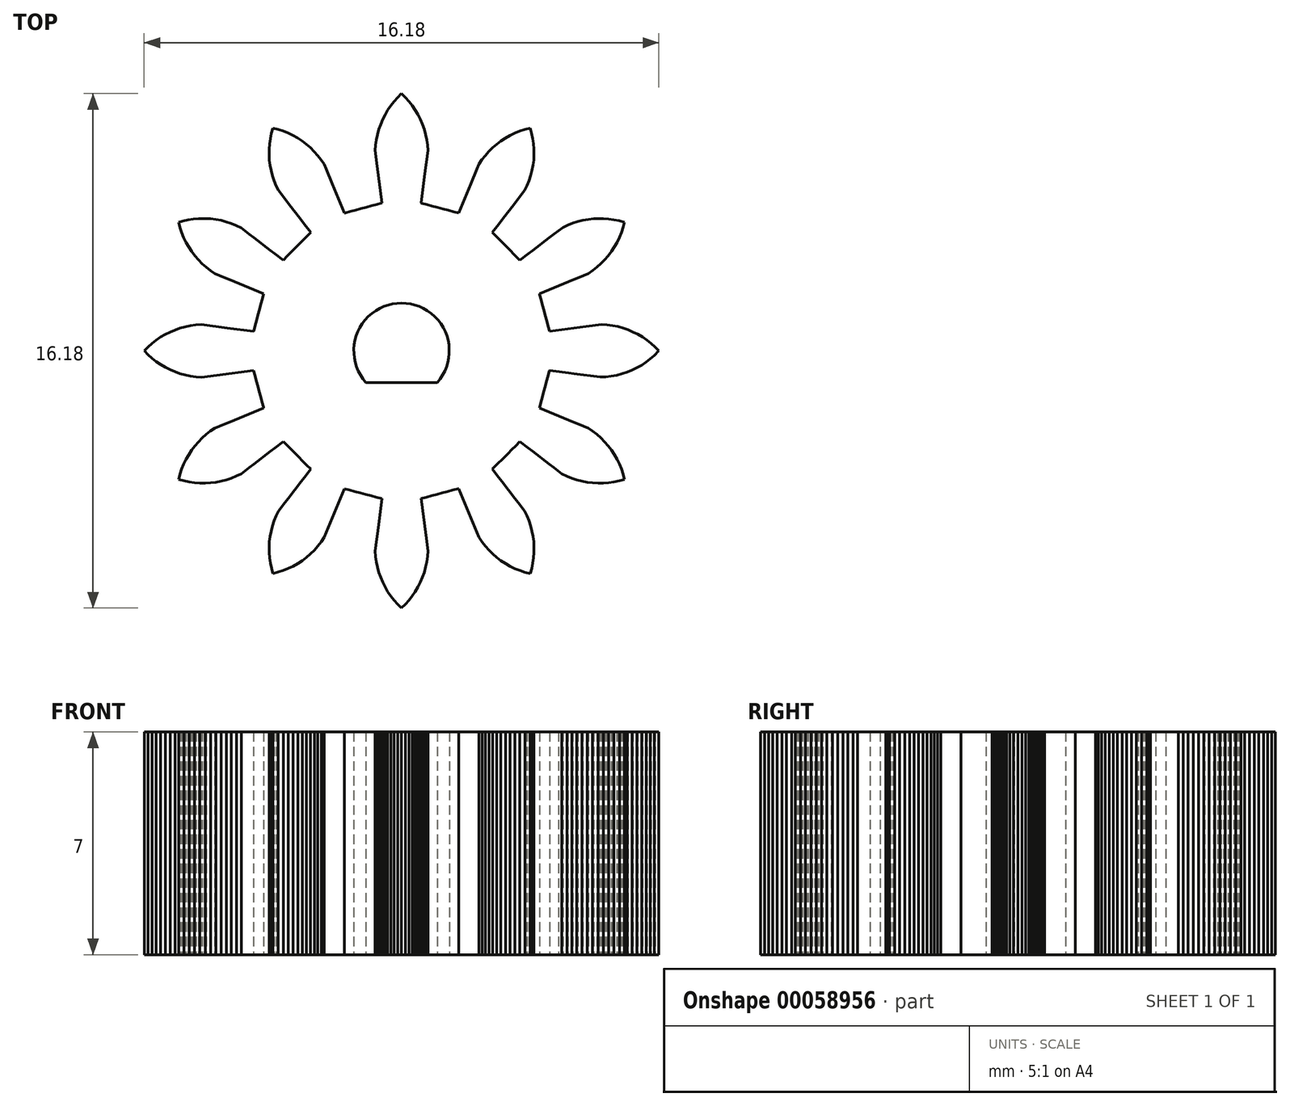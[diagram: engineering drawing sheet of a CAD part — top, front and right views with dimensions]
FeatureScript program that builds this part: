
annotation { "Feature Type Name" : "Feature", "Feature Type Description" : "" }
export const myFeature = defineFeature(function(context is Context, id is Id, definition is map)
    precondition{}
    {
        {
            var Q0;
            Q0=qCreatedBy(makeId("Top.planeOp"),FACE);
            var sketch = newSketch(context, id + "F0", { "sketchPlane" : qUnion([Q0])});
            skLineSegment(sketch, "E0", {"start": v(3.63, -0.61) * mm, "end": v(3.74, -0.63) * mm});
            skLineSegment(sketch, "E1", {"start": v(3.74, -0.63) * mm, "end": v(3.9, -0.65) * mm});
            skLineSegment(sketch, "E2", {"start": v(3.9, -0.65) * mm, "end": v(4.07, -0.67) * mm});
            skLineSegment(sketch, "E3", {"start": v(4.07, -0.67) * mm, "end": v(4.24, -0.7) * mm});
            skLineSegment(sketch, "E4", {"start": v(4.24, -0.7) * mm, "end": v(4.4, -0.71) * mm});
            skLineSegment(sketch, "E5", {"start": v(4.4, -0.71) * mm, "end": v(4.57, -0.74) * mm});
            skLineSegment(sketch, "E6", {"start": v(4.57, -0.74) * mm, "end": v(4.73, -0.76) * mm});
            skLineSegment(sketch, "E7", {"start": v(4.73, -0.76) * mm, "end": v(4.9, -0.78) * mm});
            skLineSegment(sketch, "E8", {"start": v(4.9, -0.78) * mm, "end": v(5.06, -0.8) * mm});
            skLineSegment(sketch, "E9", {"start": v(5.06, -0.8) * mm, "end": v(5.23, -0.82) * mm});
            skLineSegment(sketch, "E10", {"start": v(5.23, -0.82) * mm, "end": v(5.4, -0.82) * mm});
            skLineSegment(sketch, "E11", {"start": v(5.4, -0.82) * mm, "end": v(5.57, -0.8) * mm});
            skLineSegment(sketch, "E12", {"start": v(5.57, -0.8) * mm, "end": v(5.75, -0.77) * mm});
            skLineSegment(sketch, "E13", {"start": v(5.75, -0.77) * mm, "end": v(5.92, -0.72) * mm});
            skLineSegment(sketch, "E14", {"start": v(5.92, -0.72) * mm, "end": v(6.07, -0.67) * mm});
            skLineSegment(sketch, "E15", {"start": v(6.07, -0.67) * mm, "end": v(6.23, -0.6) * mm});
            skLineSegment(sketch, "E16", {"start": v(6.23, -0.6) * mm, "end": v(6.38, -0.53) * mm});
            skLineSegment(sketch, "E17", {"start": v(6.38, -0.53) * mm, "end": v(6.53, -0.45) * mm});
            skLineSegment(sketch, "E18", {"start": v(6.53, -0.45) * mm, "end": v(6.67, -0.36) * mm});
            skLineSegment(sketch, "E19", {"start": v(6.67, -0.36) * mm, "end": v(6.8, -0.25) * mm});
            skLineSegment(sketch, "E20", {"start": v(6.8, -0.25) * mm, "end": v(6.93, -0.14) * mm});
            skLineSegment(sketch, "E21", {"start": v(6.93, -0.14) * mm, "end": v(7.05, -0.02) * mm});
            skLineSegment(sketch, "E22", {"start": v(7.05, -0.02) * mm, "end": v(7.07, 0) * mm});
            skLineSegment(sketch, "E23", {"start": v(7.07, 0) * mm, "end": v(6.95, 0.12) * mm});
            skLineSegment(sketch, "E24", {"start": v(6.95, 0.12) * mm, "end": v(6.83, 0.23) * mm});
            skLineSegment(sketch, "E25", {"start": v(6.83, 0.23) * mm, "end": v(6.7, 0.34) * mm});
            skLineSegment(sketch, "E26", {"start": v(6.7, 0.34) * mm, "end": v(6.56, 0.43) * mm});
            skLineSegment(sketch, "E27", {"start": v(6.56, 0.43) * mm, "end": v(6.4, 0.52) * mm});
            skLineSegment(sketch, "E28", {"start": v(6.4, 0.52) * mm, "end": v(6.26, 0.6) * mm});
            skLineSegment(sketch, "E29", {"start": v(6.26, 0.6) * mm, "end": v(6.1, 0.66) * mm});
            skLineSegment(sketch, "E30", {"start": v(6.1, 0.66) * mm, "end": v(5.95, 0.72) * mm});
            skLineSegment(sketch, "E31", {"start": v(5.95, 0.72) * mm, "end": v(5.78, 0.76) * mm});
            skLineSegment(sketch, "E32", {"start": v(5.78, 0.76) * mm, "end": v(5.62, 0.8) * mm});
            skLineSegment(sketch, "E33", {"start": v(5.62, 0.8) * mm, "end": v(5.45, 0.82) * mm});
            skLineSegment(sketch, "E34", {"start": v(5.45, 0.82) * mm, "end": v(5.28, 0.83) * mm});
            skLineSegment(sketch, "E35", {"start": v(5.28, 0.83) * mm, "end": v(5.12, 0.8) * mm});
            skLineSegment(sketch, "E36", {"start": v(5.12, 0.8) * mm, "end": v(4.95, 0.79) * mm});
            skLineSegment(sketch, "E37", {"start": v(4.95, 0.79) * mm, "end": v(4.79, 0.76) * mm});
            skLineSegment(sketch, "E38", {"start": v(4.79, 0.76) * mm, "end": v(4.62, 0.74) * mm});
            skLineSegment(sketch, "E39", {"start": v(4.62, 0.74) * mm, "end": v(4.46, 0.72) * mm});
            skLineSegment(sketch, "E40", {"start": v(4.46, 0.72) * mm, "end": v(4.3, 0.7) * mm});
            skLineSegment(sketch, "E41", {"start": v(4.3, 0.7) * mm, "end": v(4.13, 0.68) * mm});
            skLineSegment(sketch, "E42", {"start": v(4.13, 0.68) * mm, "end": v(3.96, 0.66) * mm});
            skLineSegment(sketch, "E43", {"start": v(3.96, 0.66) * mm, "end": v(3.8, 0.63) * mm});
            skLineSegment(sketch, "E44", {"start": v(3.8, 0.63) * mm, "end": v(3.63, 0.61) * mm});
            skLineSegment(sketch, "E45", {"start": v(3.63, 0.61) * mm, "end": v(3.59, 0.78) * mm});
            skLineSegment(sketch, "E46", {"start": v(3.59, 0.78) * mm, "end": v(3.54, 0.94) * mm});
            skLineSegment(sketch, "E47", {"start": v(3.54, 0.94) * mm, "end": v(3.5, 1.11) * mm});
            skLineSegment(sketch, "E48", {"start": v(3.5, 1.11) * mm, "end": v(3.45, 1.28) * mm});
            skLineSegment(sketch, "E49", {"start": v(3.45, 1.28) * mm, "end": v(3.4, 1.44) * mm});
            skLineSegment(sketch, "E50", {"start": v(3.4, 1.44) * mm, "end": v(3.37, 1.6) * mm});
            skLineSegment(sketch, "E51", {"start": v(3.37, 1.6) * mm, "end": v(3.32, 1.78) * mm});
            skLineSegment(sketch, "E52", {"start": v(3.32, 1.78) * mm, "end": v(3.32, 1.8) * mm});
            skLineSegment(sketch, "E53", {"start": v(3.32, 1.8) * mm, "end": v(3.47, 1.86) * mm});
            skLineSegment(sketch, "E54", {"start": v(3.47, 1.86) * mm, "end": v(3.62, 1.92) * mm});
            skLineSegment(sketch, "E55", {"start": v(3.62, 1.92) * mm, "end": v(3.78, 1.99) * mm});
            skLineSegment(sketch, "E56", {"start": v(3.78, 1.99) * mm, "end": v(3.93, 2.05) * mm});
            skLineSegment(sketch, "E57", {"start": v(3.93, 2.05) * mm, "end": v(4.08, 2.11) * mm});
            skLineSegment(sketch, "E58", {"start": v(4.08, 2.11) * mm, "end": v(4.24, 2.18) * mm});
            skLineSegment(sketch, "E59", {"start": v(4.24, 2.18) * mm, "end": v(4.4, 2.24) * mm});
            skLineSegment(sketch, "E60", {"start": v(4.4, 2.24) * mm, "end": v(4.55, 2.3) * mm});
            skLineSegment(sketch, "E61", {"start": v(4.55, 2.3) * mm, "end": v(4.7, 2.37) * mm});
            skLineSegment(sketch, "E62", {"start": v(4.7, 2.37) * mm, "end": v(4.85, 2.43) * mm});
            skLineSegment(sketch, "E63", {"start": v(4.85, 2.43) * mm, "end": v(5, 2.53) * mm});
            skLineSegment(sketch, "E64", {"start": v(5, 2.53) * mm, "end": v(5.13, 2.63) * mm});
            skLineSegment(sketch, "E65", {"start": v(5.13, 2.63) * mm, "end": v(5.25, 2.74) * mm});
            skLineSegment(sketch, "E66", {"start": v(5.25, 2.74) * mm, "end": v(5.37, 2.86) * mm});
            skLineSegment(sketch, "E67", {"start": v(5.37, 2.86) * mm, "end": v(5.48, 3) * mm});
            skLineSegment(sketch, "E68", {"start": v(5.48, 3) * mm, "end": v(5.58, 3.12) * mm});
            skLineSegment(sketch, "E69", {"start": v(5.58, 3.12) * mm, "end": v(5.68, 3.27) * mm});
            skLineSegment(sketch, "E70", {"start": v(5.68, 3.27) * mm, "end": v(5.76, 3.41) * mm});
            skLineSegment(sketch, "E71", {"start": v(5.76, 3.41) * mm, "end": v(5.83, 3.57) * mm});
            skLineSegment(sketch, "E72", {"start": v(5.83, 3.57) * mm, "end": v(5.9, 3.72) * mm});
            skLineSegment(sketch, "E73", {"start": v(5.9, 3.72) * mm, "end": v(5.95, 3.88) * mm});
            skLineSegment(sketch, "E74", {"start": v(5.95, 3.88) * mm, "end": v(5.99, 4.04) * mm});
            skLineSegment(sketch, "E75", {"start": v(5.99, 4.04) * mm, "end": v(5.82, 4.09) * mm});
            skLineSegment(sketch, "E76", {"start": v(5.82, 4.09) * mm, "end": v(5.66, 4.12) * mm});
            skLineSegment(sketch, "E77", {"start": v(5.66, 4.12) * mm, "end": v(5.49, 4.15) * mm});
            skLineSegment(sketch, "E78", {"start": v(5.49, 4.15) * mm, "end": v(5.33, 4.16) * mm});
            skLineSegment(sketch, "E79", {"start": v(5.33, 4.16) * mm, "end": v(5.2, 4.16) * mm});
            skLineSegment(sketch, "E80", {"start": v(5.2, 4.16) * mm, "end": v(5.02, 4.15) * mm});
            skLineSegment(sketch, "E81", {"start": v(5.02, 4.15) * mm, "end": v(4.85, 4.14) * mm});
            skLineSegment(sketch, "E82", {"start": v(4.85, 4.14) * mm, "end": v(4.68, 4.1) * mm});
            skLineSegment(sketch, "E83", {"start": v(4.68, 4.1) * mm, "end": v(4.52, 4.07) * mm});
            skLineSegment(sketch, "E84", {"start": v(4.52, 4.07) * mm, "end": v(4.36, 4.01) * mm});
            skLineSegment(sketch, "E85", {"start": v(4.36, 4.01) * mm, "end": v(4.2, 3.95) * mm});
            skLineSegment(sketch, "E86", {"start": v(4.2, 3.95) * mm, "end": v(4.05, 3.88) * mm});
            skLineSegment(sketch, "E87", {"start": v(4.05, 3.88) * mm, "end": v(3.91, 3.78) * mm});
            skLineSegment(sketch, "E88", {"start": v(3.91, 3.78) * mm, "end": v(3.77, 3.68) * mm});
            skLineSegment(sketch, "E89", {"start": v(3.77, 3.68) * mm, "end": v(3.63, 3.56) * mm});
            skLineSegment(sketch, "E90", {"start": v(3.63, 3.56) * mm, "end": v(3.5, 3.46) * mm});
            skLineSegment(sketch, "E91", {"start": v(3.5, 3.46) * mm, "end": v(3.36, 3.36) * mm});
            skLineSegment(sketch, "E92", {"start": v(3.36, 3.36) * mm, "end": v(3.23, 3.26) * mm});
            skLineSegment(sketch, "E93", {"start": v(3.23, 3.26) * mm, "end": v(3.1, 3.16) * mm});
            skLineSegment(sketch, "E94", {"start": v(3.1, 3.16) * mm, "end": v(2.97, 3.06) * mm});
            skLineSegment(sketch, "E95", {"start": v(2.97, 3.06) * mm, "end": v(2.84, 2.96) * mm});
            skLineSegment(sketch, "E96", {"start": v(2.84, 2.96) * mm, "end": v(2.7, 2.85) * mm});
            skLineSegment(sketch, "E97", {"start": v(2.7, 2.85) * mm, "end": v(2.58, 2.98) * mm});
            skLineSegment(sketch, "E98", {"start": v(2.58, 2.98) * mm, "end": v(2.46, 3.1) * mm});
            skLineSegment(sketch, "E99", {"start": v(2.46, 3.1) * mm, "end": v(2.34, 3.22) * mm});
            skLineSegment(sketch, "E100", {"start": v(2.34, 3.22) * mm, "end": v(2.22, 3.34) * mm});
            skLineSegment(sketch, "E101", {"start": v(2.22, 3.34) * mm, "end": v(2.1, 3.46) * mm});
            skLineSegment(sketch, "E102", {"start": v(2.1, 3.46) * mm, "end": v(1.97, 3.58) * mm});
            skLineSegment(sketch, "E103", {"start": v(1.97, 3.58) * mm, "end": v(1.85, 3.7) * mm});
            skLineSegment(sketch, "E104", {"start": v(1.85, 3.7) * mm, "end": v(1.84, 3.72) * mm});
            skLineSegment(sketch, "E105", {"start": v(1.84, 3.72) * mm, "end": v(1.94, 3.85) * mm});
            skLineSegment(sketch, "E106", {"start": v(1.94, 3.85) * mm, "end": v(2.04, 3.98) * mm});
            skLineSegment(sketch, "E107", {"start": v(2.04, 3.98) * mm, "end": v(2.14, 4.12) * mm});
            skLineSegment(sketch, "E108", {"start": v(2.14, 4.12) * mm, "end": v(2.24, 4.25) * mm});
            skLineSegment(sketch, "E109", {"start": v(2.24, 4.25) * mm, "end": v(2.34, 4.38) * mm});
            skLineSegment(sketch, "E110", {"start": v(2.34, 4.38) * mm, "end": v(2.45, 4.51) * mm});
            skLineSegment(sketch, "E111", {"start": v(2.45, 4.51) * mm, "end": v(2.55, 4.64) * mm});
            skLineSegment(sketch, "E112", {"start": v(2.55, 4.64) * mm, "end": v(2.65, 4.78) * mm});
            skLineSegment(sketch, "E113", {"start": v(2.65, 4.78) * mm, "end": v(2.75, 4.9) * mm});
            skLineSegment(sketch, "E114", {"start": v(2.75, 4.9) * mm, "end": v(2.85, 5.04) * mm});
            skLineSegment(sketch, "E115", {"start": v(2.85, 5.04) * mm, "end": v(2.92, 5.2) * mm});
            skLineSegment(sketch, "E116", {"start": v(2.92, 5.2) * mm, "end": v(2.99, 5.35) * mm});
            skLineSegment(sketch, "E117", {"start": v(2.99, 5.35) * mm, "end": v(3.04, 5.51) * mm});
            skLineSegment(sketch, "E118", {"start": v(3.04, 5.51) * mm, "end": v(3.08, 5.67) * mm});
            skLineSegment(sketch, "E119", {"start": v(3.08, 5.67) * mm, "end": v(3.11, 5.84) * mm});
            skLineSegment(sketch, "E120", {"start": v(3.11, 5.84) * mm, "end": v(3.14, 6) * mm});
            skLineSegment(sketch, "E121", {"start": v(3.14, 6) * mm, "end": v(3.14, 6.18) * mm});
            skLineSegment(sketch, "E122", {"start": v(3.14, 6.18) * mm, "end": v(3.14, 6.34) * mm});
            skLineSegment(sketch, "E123", {"start": v(3.14, 6.34) * mm, "end": v(3.13, 6.51) * mm});
            skLineSegment(sketch, "E124", {"start": v(3.13, 6.51) * mm, "end": v(3.1, 6.68) * mm});
            skLineSegment(sketch, "E125", {"start": v(3.1, 6.68) * mm, "end": v(3.07, 6.85) * mm});
            skLineSegment(sketch, "E126", {"start": v(3.07, 6.85) * mm, "end": v(3.03, 7) * mm});
            skLineSegment(sketch, "E127", {"start": v(3.03, 7) * mm, "end": v(2.86, 6.96) * mm});
            skLineSegment(sketch, "E128", {"start": v(2.86, 6.96) * mm, "end": v(2.7, 6.91) * mm});
            skLineSegment(sketch, "E129", {"start": v(2.7, 6.91) * mm, "end": v(2.54, 6.85) * mm});
            skLineSegment(sketch, "E130", {"start": v(2.54, 6.85) * mm, "end": v(2.4, 6.77) * mm});
            skLineSegment(sketch, "E131", {"start": v(2.4, 6.77) * mm, "end": v(2.25, 6.69) * mm});
            skLineSegment(sketch, "E132", {"start": v(2.25, 6.69) * mm, "end": v(2.1, 6.6) * mm});
            skLineSegment(sketch, "E133", {"start": v(2.1, 6.6) * mm, "end": v(1.97, 6.5) * mm});
            skLineSegment(sketch, "E134", {"start": v(1.97, 6.5) * mm, "end": v(1.84, 6.39) * mm});
            skLineSegment(sketch, "E135", {"start": v(1.84, 6.39) * mm, "end": v(1.72, 6.27) * mm});
            skLineSegment(sketch, "E136", {"start": v(1.72, 6.27) * mm, "end": v(1.61, 6.14) * mm});
            skLineSegment(sketch, "E137", {"start": v(1.61, 6.14) * mm, "end": v(1.5, 6) * mm});
            skLineSegment(sketch, "E138", {"start": v(1.5, 6) * mm, "end": v(1.41, 5.87) * mm});
            skLineSegment(sketch, "E139", {"start": v(1.41, 5.87) * mm, "end": v(1.35, 5.72) * mm});
            skLineSegment(sketch, "E140", {"start": v(1.35, 5.72) * mm, "end": v(1.29, 5.56) * mm});
            skLineSegment(sketch, "E141", {"start": v(1.29, 5.56) * mm, "end": v(1.22, 5.4) * mm});
            skLineSegment(sketch, "E142", {"start": v(1.22, 5.4) * mm, "end": v(1.16, 5.25) * mm});
            skLineSegment(sketch, "E143", {"start": v(1.16, 5.25) * mm, "end": v(1.1, 5.1) * mm});
            skLineSegment(sketch, "E144", {"start": v(1.1, 5.1) * mm, "end": v(1.03, 4.95) * mm});
            skLineSegment(sketch, "E145", {"start": v(1.03, 4.95) * mm, "end": v(0.97, 4.8) * mm});
            skLineSegment(sketch, "E146", {"start": v(0.97, 4.8) * mm, "end": v(0.9, 4.64) * mm});
            skLineSegment(sketch, "E147", {"start": v(0.9, 4.64) * mm, "end": v(0.84, 4.49) * mm});
            skLineSegment(sketch, "E148", {"start": v(0.84, 4.49) * mm, "end": v(0.78, 4.33) * mm});
            skLineSegment(sketch, "E149", {"start": v(0.78, 4.33) * mm, "end": v(0.61, 4.38) * mm});
            skLineSegment(sketch, "E150", {"start": v(0.61, 4.38) * mm, "end": v(0.45, 4.42) * mm});
            skLineSegment(sketch, "E151", {"start": v(0.45, 4.42) * mm, "end": v(0.28, 4.47) * mm});
            skLineSegment(sketch, "E152", {"start": v(0.28, 4.47) * mm, "end": v(0.11, 4.51) * mm});
            skLineSegment(sketch, "E153", {"start": v(0.11, 4.51) * mm, "end": v(-0.05, 4.56) * mm});
            skLineSegment(sketch, "E154", {"start": v(-0.05, 4.56) * mm, "end": v(-0.22, 4.6) * mm});
            skLineSegment(sketch, "E155", {"start": v(-0.22, 4.6) * mm, "end": v(-0.39, 4.64) * mm});
            skLineSegment(sketch, "E156", {"start": v(-0.39, 4.64) * mm, "end": v(-0.4, 4.65) * mm});
            skLineSegment(sketch, "E157", {"start": v(-0.4, 4.65) * mm, "end": v(-0.38, 4.81) * mm});
            skLineSegment(sketch, "E158", {"start": v(-0.38, 4.81) * mm, "end": v(-0.36, 4.98) * mm});
            skLineSegment(sketch, "E159", {"start": v(-0.36, 4.98) * mm, "end": v(-0.34, 5.14) * mm});
            skLineSegment(sketch, "E160", {"start": v(-0.34, 5.14) * mm, "end": v(-0.32, 5.3) * mm});
            skLineSegment(sketch, "E161", {"start": v(-0.32, 5.3) * mm, "end": v(-0.3, 5.47) * mm});
            skLineSegment(sketch, "E162", {"start": v(-0.3, 5.47) * mm, "end": v(-0.27, 5.64) * mm});
            skLineSegment(sketch, "E163", {"start": v(-0.27, 5.64) * mm, "end": v(-0.25, 5.8) * mm});
            skLineSegment(sketch, "E164", {"start": v(-0.25, 5.8) * mm, "end": v(-0.23, 5.97) * mm});
            skLineSegment(sketch, "E165", {"start": v(-0.23, 5.97) * mm, "end": v(-0.2, 6.13) * mm});
            skLineSegment(sketch, "E166", {"start": v(-0.2, 6.13) * mm, "end": v(-0.19, 6.3) * mm});
            skLineSegment(sketch, "E167", {"start": v(-0.19, 6.3) * mm, "end": v(-0.2, 6.47) * mm});
            skLineSegment(sketch, "E168", {"start": v(-0.2, 6.47) * mm, "end": v(-0.22, 6.63) * mm});
            skLineSegment(sketch, "E169", {"start": v(-0.22, 6.63) * mm, "end": v(-0.26, 6.8) * mm});
            skLineSegment(sketch, "E170", {"start": v(-0.26, 6.8) * mm, "end": v(-0.3, 6.96) * mm});
            skLineSegment(sketch, "E171", {"start": v(-0.3, 6.96) * mm, "end": v(-0.36, 7.12) * mm});
            skLineSegment(sketch, "E172", {"start": v(-0.36, 7.12) * mm, "end": v(-0.42, 7.28) * mm});
            skLineSegment(sketch, "E173", {"start": v(-0.42, 7.28) * mm, "end": v(-0.5, 7.43) * mm});
            skLineSegment(sketch, "E174", {"start": v(-0.5, 7.43) * mm, "end": v(-0.58, 7.57) * mm});
            skLineSegment(sketch, "E175", {"start": v(-0.58, 7.57) * mm, "end": v(-0.68, 7.71) * mm});
            skLineSegment(sketch, "E176", {"start": v(-0.68, 7.71) * mm, "end": v(-0.78, 7.85) * mm});
            skLineSegment(sketch, "E177", {"start": v(-0.78, 7.85) * mm, "end": v(-0.9, 7.97) * mm});
            skLineSegment(sketch, "E178", {"start": v(-0.9, 7.97) * mm, "end": v(-1.02, 8.09) * mm});
            skLineSegment(sketch, "E179", {"start": v(-1.02, 8.09) * mm, "end": v(-1.14, 7.97) * mm});
            skLineSegment(sketch, "E180", {"start": v(-1.14, 7.97) * mm, "end": v(-1.25, 7.85) * mm});
            skLineSegment(sketch, "E181", {"start": v(-1.25, 7.85) * mm, "end": v(-1.36, 7.7) * mm});
            skLineSegment(sketch, "E182", {"start": v(-1.36, 7.7) * mm, "end": v(-1.45, 7.57) * mm});
            skLineSegment(sketch, "E183", {"start": v(-1.45, 7.57) * mm, "end": v(-1.54, 7.42) * mm});
            skLineSegment(sketch, "E184", {"start": v(-1.54, 7.42) * mm, "end": v(-1.61, 7.28) * mm});
            skLineSegment(sketch, "E185", {"start": v(-1.61, 7.28) * mm, "end": v(-1.68, 7.12) * mm});
            skLineSegment(sketch, "E186", {"start": v(-1.68, 7.12) * mm, "end": v(-1.73, 6.96) * mm});
            skLineSegment(sketch, "E187", {"start": v(-1.73, 6.96) * mm, "end": v(-1.78, 6.8) * mm});
            skLineSegment(sketch, "E188", {"start": v(-1.78, 6.8) * mm, "end": v(-1.81, 6.63) * mm});
            skLineSegment(sketch, "E189", {"start": v(-1.81, 6.63) * mm, "end": v(-1.83, 6.46) * mm});
            skLineSegment(sketch, "E190", {"start": v(-1.83, 6.46) * mm, "end": v(-1.85, 6.3) * mm});
            skLineSegment(sketch, "E191", {"start": v(-1.85, 6.3) * mm, "end": v(-1.82, 6.13) * mm});
            skLineSegment(sketch, "E192", {"start": v(-1.82, 6.13) * mm, "end": v(-1.8, 5.97) * mm});
            skLineSegment(sketch, "E193", {"start": v(-1.8, 5.97) * mm, "end": v(-1.78, 5.8) * mm});
            skLineSegment(sketch, "E194", {"start": v(-1.78, 5.8) * mm, "end": v(-1.76, 5.64) * mm});
            skLineSegment(sketch, "E195", {"start": v(-1.76, 5.64) * mm, "end": v(-1.74, 5.47) * mm});
            skLineSegment(sketch, "E196", {"start": v(-1.74, 5.47) * mm, "end": v(-1.72, 5.3) * mm});
            skLineSegment(sketch, "E197", {"start": v(-1.72, 5.3) * mm, "end": v(-1.7, 5.14) * mm});
            skLineSegment(sketch, "E198", {"start": v(-1.7, 5.14) * mm, "end": v(-1.67, 4.98) * mm});
            skLineSegment(sketch, "E199", {"start": v(-1.67, 4.98) * mm, "end": v(-1.65, 4.81) * mm});
            skLineSegment(sketch, "E200", {"start": v(-1.65, 4.81) * mm, "end": v(-1.63, 4.65) * mm});
            skLineSegment(sketch, "E201", {"start": v(-1.63, 4.65) * mm, "end": v(-1.8, 4.6) * mm});
            skLineSegment(sketch, "E202", {"start": v(-1.8, 4.6) * mm, "end": v(-1.96, 4.56) * mm});
            skLineSegment(sketch, "E203", {"start": v(-1.96, 4.56) * mm, "end": v(-2.13, 4.52) * mm});
            skLineSegment(sketch, "E204", {"start": v(-2.13, 4.52) * mm, "end": v(-2.3, 4.47) * mm});
            skLineSegment(sketch, "E205", {"start": v(-2.3, 4.47) * mm, "end": v(-2.46, 4.43) * mm});
            skLineSegment(sketch, "E206", {"start": v(-2.46, 4.43) * mm, "end": v(-2.63, 4.38) * mm});
            skLineSegment(sketch, "E207", {"start": v(-2.63, 4.38) * mm, "end": v(-2.8, 4.34) * mm});
            skLineSegment(sketch, "E208", {"start": v(-2.8, 4.34) * mm, "end": v(-2.81, 4.33) * mm});
            skLineSegment(sketch, "E209", {"start": v(-2.81, 4.33) * mm, "end": v(-2.88, 4.49) * mm});
            skLineSegment(sketch, "E210", {"start": v(-2.88, 4.49) * mm, "end": v(-2.94, 4.64) * mm});
            skLineSegment(sketch, "E211", {"start": v(-2.94, 4.64) * mm, "end": v(-3, 4.8) * mm});
            skLineSegment(sketch, "E212", {"start": v(-3, 4.8) * mm, "end": v(-3.07, 4.95) * mm});
            skLineSegment(sketch, "E213", {"start": v(-3.07, 4.95) * mm, "end": v(-3.13, 5.1) * mm});
            skLineSegment(sketch, "E214", {"start": v(-3.13, 5.1) * mm, "end": v(-3.2, 5.25) * mm});
            skLineSegment(sketch, "E215", {"start": v(-3.2, 5.25) * mm, "end": v(-3.26, 5.4) * mm});
            skLineSegment(sketch, "E216", {"start": v(-3.26, 5.4) * mm, "end": v(-3.32, 5.56) * mm});
            skLineSegment(sketch, "E217", {"start": v(-3.32, 5.56) * mm, "end": v(-3.38, 5.72) * mm});
            skLineSegment(sketch, "E218", {"start": v(-3.38, 5.72) * mm, "end": v(-3.45, 5.87) * mm});
            skLineSegment(sketch, "E219", {"start": v(-3.45, 5.87) * mm, "end": v(-3.55, 6.01) * mm});
            skLineSegment(sketch, "E220", {"start": v(-3.55, 6.01) * mm, "end": v(-3.65, 6.14) * mm});
            skLineSegment(sketch, "E221", {"start": v(-3.65, 6.14) * mm, "end": v(-3.76, 6.27) * mm});
            skLineSegment(sketch, "E222", {"start": v(-3.76, 6.27) * mm, "end": v(-3.88, 6.39) * mm});
            skLineSegment(sketch, "E223", {"start": v(-3.88, 6.39) * mm, "end": v(-4, 6.5) * mm});
            skLineSegment(sketch, "E224", {"start": v(-4, 6.5) * mm, "end": v(-4.14, 6.6) * mm});
            skLineSegment(sketch, "E225", {"start": v(-4.14, 6.6) * mm, "end": v(-4.29, 6.7) * mm});
            skLineSegment(sketch, "E226", {"start": v(-4.29, 6.7) * mm, "end": v(-4.43, 6.77) * mm});
            skLineSegment(sketch, "E227", {"start": v(-4.43, 6.77) * mm, "end": v(-4.58, 6.85) * mm});
            skLineSegment(sketch, "E228", {"start": v(-4.58, 6.85) * mm, "end": v(-4.74, 6.91) * mm});
            skLineSegment(sketch, "E229", {"start": v(-4.74, 6.91) * mm, "end": v(-4.9, 6.96) * mm});
            skLineSegment(sketch, "E230", {"start": v(-4.9, 6.96) * mm, "end": v(-5.06, 7) * mm});
            skLineSegment(sketch, "E231", {"start": v(-5.06, 7) * mm, "end": v(-5.1, 6.84) * mm});
            skLineSegment(sketch, "E232", {"start": v(-5.1, 6.84) * mm, "end": v(-5.14, 6.68) * mm});
            skLineSegment(sketch, "E233", {"start": v(-5.14, 6.68) * mm, "end": v(-5.16, 6.5) * mm});
            skLineSegment(sketch, "E234", {"start": v(-5.16, 6.5) * mm, "end": v(-5.18, 6.34) * mm});
            skLineSegment(sketch, "E235", {"start": v(-5.18, 6.34) * mm, "end": v(-5.18, 6.17) * mm});
            skLineSegment(sketch, "E236", {"start": v(-5.18, 6.17) * mm, "end": v(-5.17, 6) * mm});
            skLineSegment(sketch, "E237", {"start": v(-5.17, 6) * mm, "end": v(-5.15, 5.83) * mm});
            skLineSegment(sketch, "E238", {"start": v(-5.15, 5.83) * mm, "end": v(-5.12, 5.67) * mm});
            skLineSegment(sketch, "E239", {"start": v(-5.12, 5.67) * mm, "end": v(-5.07, 5.5) * mm});
            skLineSegment(sketch, "E240", {"start": v(-5.07, 5.5) * mm, "end": v(-5.02, 5.35) * mm});
            skLineSegment(sketch, "E241", {"start": v(-5.02, 5.35) * mm, "end": v(-4.96, 5.19) * mm});
            skLineSegment(sketch, "E242", {"start": v(-4.96, 5.19) * mm, "end": v(-4.88, 5.04) * mm});
            skLineSegment(sketch, "E243", {"start": v(-4.88, 5.04) * mm, "end": v(-4.78, 4.9) * mm});
            skLineSegment(sketch, "E244", {"start": v(-4.78, 4.9) * mm, "end": v(-4.68, 4.78) * mm});
            skLineSegment(sketch, "E245", {"start": v(-4.68, 4.78) * mm, "end": v(-4.58, 4.64) * mm});
            skLineSegment(sketch, "E246", {"start": v(-4.58, 4.64) * mm, "end": v(-4.48, 4.51) * mm});
            skLineSegment(sketch, "E247", {"start": v(-4.48, 4.51) * mm, "end": v(-4.38, 4.38) * mm});
            skLineSegment(sketch, "E248", {"start": v(-4.38, 4.38) * mm, "end": v(-4.28, 4.25) * mm});
            skLineSegment(sketch, "E249", {"start": v(-4.28, 4.25) * mm, "end": v(-4.18, 4.12) * mm});
            skLineSegment(sketch, "E250", {"start": v(-4.18, 4.12) * mm, "end": v(-4.07, 3.98) * mm});
            skLineSegment(sketch, "E251", {"start": v(-4.07, 3.98) * mm, "end": v(-3.97, 3.85) * mm});
            skLineSegment(sketch, "E252", {"start": v(-3.97, 3.85) * mm, "end": v(-3.87, 3.72) * mm});
            skLineSegment(sketch, "E253", {"start": v(-3.87, 3.72) * mm, "end": v(-4, 3.6) * mm});
            skLineSegment(sketch, "E254", {"start": v(-4, 3.6) * mm, "end": v(-4.12, 3.48) * mm});
            skLineSegment(sketch, "E255", {"start": v(-4.12, 3.48) * mm, "end": v(-4.24, 3.36) * mm});
            skLineSegment(sketch, "E256", {"start": v(-4.24, 3.36) * mm, "end": v(-4.36, 3.23) * mm});
            skLineSegment(sketch, "E257", {"start": v(-4.36, 3.23) * mm, "end": v(-4.48, 3.11) * mm});
            skLineSegment(sketch, "E258", {"start": v(-4.48, 3.11) * mm, "end": v(-4.6, 3) * mm});
            skLineSegment(sketch, "E259", {"start": v(-4.6, 3) * mm, "end": v(-4.72, 2.87) * mm});
            skLineSegment(sketch, "E260", {"start": v(-4.72, 2.87) * mm, "end": v(-4.74, 2.85) * mm});
            skLineSegment(sketch, "E261", {"start": v(-4.74, 2.85) * mm, "end": v(-4.87, 2.96) * mm});
            skLineSegment(sketch, "E262", {"start": v(-4.87, 2.96) * mm, "end": v(-5, 3.06) * mm});
            skLineSegment(sketch, "E263", {"start": v(-5, 3.06) * mm, "end": v(-5.13, 3.16) * mm});
            skLineSegment(sketch, "E264", {"start": v(-5.13, 3.16) * mm, "end": v(-5.27, 3.26) * mm});
            skLineSegment(sketch, "E265", {"start": v(-5.27, 3.26) * mm, "end": v(-5.4, 3.36) * mm});
            skLineSegment(sketch, "E266", {"start": v(-5.4, 3.36) * mm, "end": v(-5.53, 3.46) * mm});
            skLineSegment(sketch, "E267", {"start": v(-5.53, 3.46) * mm, "end": v(-5.66, 3.56) * mm});
            skLineSegment(sketch, "E268", {"start": v(-5.66, 3.56) * mm, "end": v(-5.8, 3.66) * mm});
            skLineSegment(sketch, "E269", {"start": v(-5.8, 3.66) * mm, "end": v(-5.93, 3.77) * mm});
            skLineSegment(sketch, "E270", {"start": v(-5.93, 3.77) * mm, "end": v(-6.06, 3.87) * mm});
            skLineSegment(sketch, "E271", {"start": v(-6.06, 3.87) * mm, "end": v(-6.21, 3.94) * mm});
            skLineSegment(sketch, "E272", {"start": v(-6.21, 3.94) * mm, "end": v(-6.37, 4) * mm});
            skLineSegment(sketch, "E273", {"start": v(-6.37, 4) * mm, "end": v(-6.53, 4.06) * mm});
            skLineSegment(sketch, "E274", {"start": v(-6.53, 4.06) * mm, "end": v(-6.69, 4.1) * mm});
            skLineSegment(sketch, "E275", {"start": v(-6.69, 4.1) * mm, "end": v(-6.86, 4.13) * mm});
            skLineSegment(sketch, "E276", {"start": v(-6.86, 4.13) * mm, "end": v(-7.02, 4.15) * mm});
            skLineSegment(sketch, "E277", {"start": v(-7.02, 4.15) * mm, "end": v(-7.2, 4.16) * mm});
            skLineSegment(sketch, "E278", {"start": v(-7.2, 4.16) * mm, "end": v(-7.22, 4.16) * mm});
            skLineSegment(sketch, "E279", {"start": v(-7.22, 4.16) * mm, "end": v(-7.4, 4.16) * mm});
            skLineSegment(sketch, "E280", {"start": v(-7.4, 4.16) * mm, "end": v(-7.56, 4.14) * mm});
            skLineSegment(sketch, "E281", {"start": v(-7.56, 4.14) * mm, "end": v(-7.73, 4.12) * mm});
            skLineSegment(sketch, "E282", {"start": v(-7.73, 4.12) * mm, "end": v(-7.9, 4.08) * mm});
            skLineSegment(sketch, "E283", {"start": v(-7.9, 4.08) * mm, "end": v(-8.02, 4.04) * mm});
            skLineSegment(sketch, "E284", {"start": v(-8.02, 4.04) * mm, "end": v(-7.98, 3.88) * mm});
            skLineSegment(sketch, "E285", {"start": v(-7.98, 3.88) * mm, "end": v(-7.93, 3.72) * mm});
            skLineSegment(sketch, "E286", {"start": v(-7.93, 3.72) * mm, "end": v(-7.86, 3.56) * mm});
            skLineSegment(sketch, "E287", {"start": v(-7.86, 3.56) * mm, "end": v(-7.8, 3.41) * mm});
            skLineSegment(sketch, "E288", {"start": v(-7.8, 3.41) * mm, "end": v(-7.7, 3.26) * mm});
            skLineSegment(sketch, "E289", {"start": v(-7.7, 3.26) * mm, "end": v(-7.62, 3.12) * mm});
            skLineSegment(sketch, "E290", {"start": v(-7.62, 3.12) * mm, "end": v(-7.51, 2.99) * mm});
            skLineSegment(sketch, "E291", {"start": v(-7.51, 2.99) * mm, "end": v(-7.4, 2.86) * mm});
            skLineSegment(sketch, "E292", {"start": v(-7.4, 2.86) * mm, "end": v(-7.28, 2.74) * mm});
            skLineSegment(sketch, "E293", {"start": v(-7.28, 2.74) * mm, "end": v(-7.16, 2.63) * mm});
            skLineSegment(sketch, "E294", {"start": v(-7.16, 2.63) * mm, "end": v(-7.02, 2.52) * mm});
            skLineSegment(sketch, "E295", {"start": v(-7.02, 2.52) * mm, "end": v(-6.89, 2.43) * mm});
            skLineSegment(sketch, "E296", {"start": v(-6.89, 2.43) * mm, "end": v(-6.73, 2.37) * mm});
            skLineSegment(sketch, "E297", {"start": v(-6.73, 2.37) * mm, "end": v(-6.58, 2.3) * mm});
            skLineSegment(sketch, "E298", {"start": v(-6.58, 2.3) * mm, "end": v(-6.43, 2.24) * mm});
            skLineSegment(sketch, "E299", {"start": v(-6.43, 2.24) * mm, "end": v(-6.27, 2.18) * mm});
            skLineSegment(sketch, "E300", {"start": v(-6.27, 2.18) * mm, "end": v(-6.12, 2.11) * mm});
            skLineSegment(sketch, "E301", {"start": v(-6.12, 2.11) * mm, "end": v(-5.96, 2.05) * mm});
            skLineSegment(sketch, "E302", {"start": v(-5.96, 2.05) * mm, "end": v(-5.81, 1.99) * mm});
            skLineSegment(sketch, "E303", {"start": v(-5.81, 1.99) * mm, "end": v(-5.66, 1.92) * mm});
            skLineSegment(sketch, "E304", {"start": v(-5.66, 1.92) * mm, "end": v(-5.5, 1.86) * mm});
            skLineSegment(sketch, "E305", {"start": v(-5.5, 1.86) * mm, "end": v(-5.35, 1.8) * mm});
            skLineSegment(sketch, "E306", {"start": v(-5.35, 1.8) * mm, "end": v(-5.4, 1.63) * mm});
            skLineSegment(sketch, "E307", {"start": v(-5.4, 1.63) * mm, "end": v(-5.44, 1.46) * mm});
            skLineSegment(sketch, "E308", {"start": v(-5.44, 1.46) * mm, "end": v(-5.48, 1.3) * mm});
            skLineSegment(sketch, "E309", {"start": v(-5.48, 1.3) * mm, "end": v(-5.53, 1.13) * mm});
            skLineSegment(sketch, "E310", {"start": v(-5.53, 1.13) * mm, "end": v(-5.57, 0.96) * mm});
            skLineSegment(sketch, "E311", {"start": v(-5.57, 0.96) * mm, "end": v(-5.62, 0.8) * mm});
            skLineSegment(sketch, "E312", {"start": v(-5.62, 0.8) * mm, "end": v(-5.66, 0.63) * mm});
            skLineSegment(sketch, "E313", {"start": v(-5.66, 0.63) * mm, "end": v(-5.67, 0.61) * mm});
            skLineSegment(sketch, "E314", {"start": v(-5.67, 0.61) * mm, "end": v(-5.83, 0.63) * mm});
            skLineSegment(sketch, "E315", {"start": v(-5.83, 0.63) * mm, "end": v(-6, 0.66) * mm});
            skLineSegment(sketch, "E316", {"start": v(-6, 0.66) * mm, "end": v(-6.16, 0.68) * mm});
            skLineSegment(sketch, "E317", {"start": v(-6.16, 0.68) * mm, "end": v(-6.33, 0.7) * mm});
            skLineSegment(sketch, "E318", {"start": v(-6.33, 0.7) * mm, "end": v(-6.5, 0.72) * mm});
            skLineSegment(sketch, "E319", {"start": v(-6.5, 0.72) * mm, "end": v(-6.66, 0.74) * mm});
            skLineSegment(sketch, "E320", {"start": v(-6.66, 0.74) * mm, "end": v(-6.82, 0.76) * mm});
            skLineSegment(sketch, "E321", {"start": v(-6.82, 0.76) * mm, "end": v(-6.99, 0.79) * mm});
            skLineSegment(sketch, "E322", {"start": v(-6.99, 0.79) * mm, "end": v(-7.15, 0.8) * mm});
            skLineSegment(sketch, "E323", {"start": v(-7.15, 0.8) * mm, "end": v(-7.32, 0.83) * mm});
            skLineSegment(sketch, "E324", {"start": v(-7.32, 0.83) * mm, "end": v(-7.49, 0.82) * mm});
            skLineSegment(sketch, "E325", {"start": v(-7.49, 0.82) * mm, "end": v(-7.65, 0.8) * mm});
            skLineSegment(sketch, "E326", {"start": v(-7.65, 0.8) * mm, "end": v(-7.82, 0.76) * mm});
            skLineSegment(sketch, "E327", {"start": v(-7.82, 0.76) * mm, "end": v(-7.98, 0.72) * mm});
            skLineSegment(sketch, "E328", {"start": v(-7.98, 0.72) * mm, "end": v(-8.14, 0.66) * mm});
            skLineSegment(sketch, "E329", {"start": v(-8.14, 0.66) * mm, "end": v(-8.3, 0.6) * mm});
            skLineSegment(sketch, "E330", {"start": v(-8.3, 0.6) * mm, "end": v(-8.45, 0.52) * mm});
            skLineSegment(sketch, "E331", {"start": v(-8.45, 0.52) * mm, "end": v(-8.59, 0.43) * mm});
            skLineSegment(sketch, "E332", {"start": v(-8.59, 0.43) * mm, "end": v(-8.73, 0.33) * mm});
            skLineSegment(sketch, "E333", {"start": v(-8.73, 0.33) * mm, "end": v(-8.86, 0.23) * mm});
            skLineSegment(sketch, "E334", {"start": v(-8.86, 0.23) * mm, "end": v(-8.99, 0.12) * mm});
            skLineSegment(sketch, "E335", {"start": v(-8.99, 0.12) * mm, "end": v(-9.1, 0) * mm});
            skLineSegment(sketch, "E336", {"start": v(-9.1, 0) * mm, "end": v(-8.98, -0.12) * mm});
            skLineSegment(sketch, "E337", {"start": v(-8.98, -0.12) * mm, "end": v(-8.86, -0.23) * mm});
            skLineSegment(sketch, "E338", {"start": v(-8.86, -0.23) * mm, "end": v(-8.73, -0.34) * mm});
            skLineSegment(sketch, "E339", {"start": v(-8.73, -0.34) * mm, "end": v(-8.59, -0.43) * mm});
            skLineSegment(sketch, "E340", {"start": v(-8.59, -0.43) * mm, "end": v(-8.44, -0.52) * mm});
            skLineSegment(sketch, "E341", {"start": v(-8.44, -0.52) * mm, "end": v(-8.3, -0.6) * mm});
            skLineSegment(sketch, "E342", {"start": v(-8.3, -0.6) * mm, "end": v(-8.14, -0.66) * mm});
            skLineSegment(sketch, "E343", {"start": v(-8.14, -0.66) * mm, "end": v(-7.98, -0.72) * mm});
            skLineSegment(sketch, "E344", {"start": v(-7.98, -0.72) * mm, "end": v(-7.81, -0.76) * mm});
            skLineSegment(sketch, "E345", {"start": v(-7.81, -0.76) * mm, "end": v(-7.65, -0.8) * mm});
            skLineSegment(sketch, "E346", {"start": v(-7.65, -0.8) * mm, "end": v(-7.48, -0.82) * mm});
            skLineSegment(sketch, "E347", {"start": v(-7.48, -0.82) * mm, "end": v(-7.32, -0.83) * mm});
            skLineSegment(sketch, "E348", {"start": v(-7.32, -0.83) * mm, "end": v(-7.15, -0.8) * mm});
            skLineSegment(sketch, "E349", {"start": v(-7.15, -0.8) * mm, "end": v(-6.99, -0.79) * mm});
            skLineSegment(sketch, "E350", {"start": v(-6.99, -0.79) * mm, "end": v(-6.82, -0.76) * mm});
            skLineSegment(sketch, "E351", {"start": v(-6.82, -0.76) * mm, "end": v(-6.66, -0.74) * mm});
            skLineSegment(sketch, "E352", {"start": v(-6.66, -0.74) * mm, "end": v(-6.5, -0.72) * mm});
            skLineSegment(sketch, "E353", {"start": v(-6.5, -0.72) * mm, "end": v(-6.33, -0.7) * mm});
            skLineSegment(sketch, "E354", {"start": v(-6.33, -0.7) * mm, "end": v(-6.16, -0.68) * mm});
            skLineSegment(sketch, "E355", {"start": v(-6.16, -0.68) * mm, "end": v(-6, -0.66) * mm});
            skLineSegment(sketch, "E356", {"start": v(-6, -0.66) * mm, "end": v(-5.83, -0.63) * mm});
            skLineSegment(sketch, "E357", {"start": v(-5.83, -0.63) * mm, "end": v(-5.67, -0.61) * mm});
            skLineSegment(sketch, "E358", {"start": v(-5.67, -0.61) * mm, "end": v(-5.62, -0.78) * mm});
            skLineSegment(sketch, "E359", {"start": v(-5.62, -0.78) * mm, "end": v(-5.58, -0.94) * mm});
            skLineSegment(sketch, "E360", {"start": v(-5.58, -0.94) * mm, "end": v(-5.53, -1.11) * mm});
            skLineSegment(sketch, "E361", {"start": v(-5.53, -1.11) * mm, "end": v(-5.49, -1.28) * mm});
            skLineSegment(sketch, "E362", {"start": v(-5.49, -1.28) * mm, "end": v(-5.44, -1.44) * mm});
            skLineSegment(sketch, "E363", {"start": v(-5.44, -1.44) * mm, "end": v(-5.4, -1.6) * mm});
            skLineSegment(sketch, "E364", {"start": v(-5.4, -1.6) * mm, "end": v(-5.35, -1.78) * mm});
            skLineSegment(sketch, "E365", {"start": v(-5.35, -1.78) * mm, "end": v(-5.35, -1.8) * mm});
            skLineSegment(sketch, "E366", {"start": v(-5.35, -1.8) * mm, "end": v(-5.5, -1.86) * mm});
            skLineSegment(sketch, "E367", {"start": v(-5.5, -1.86) * mm, "end": v(-5.66, -1.92) * mm});
            skLineSegment(sketch, "E368", {"start": v(-5.66, -1.92) * mm, "end": v(-5.81, -1.99) * mm});
            skLineSegment(sketch, "E369", {"start": v(-5.81, -1.99) * mm, "end": v(-5.96, -2.05) * mm});
            skLineSegment(sketch, "E370", {"start": v(-5.96, -2.05) * mm, "end": v(-6.12, -2.11) * mm});
            skLineSegment(sketch, "E371", {"start": v(-6.12, -2.11) * mm, "end": v(-6.27, -2.18) * mm});
            skLineSegment(sketch, "E372", {"start": v(-6.27, -2.18) * mm, "end": v(-6.43, -2.24) * mm});
            skLineSegment(sketch, "E373", {"start": v(-6.43, -2.24) * mm, "end": v(-6.58, -2.3) * mm});
            skLineSegment(sketch, "E374", {"start": v(-6.58, -2.3) * mm, "end": v(-6.73, -2.37) * mm});
            skLineSegment(sketch, "E375", {"start": v(-6.73, -2.37) * mm, "end": v(-6.89, -2.43) * mm});
            skLineSegment(sketch, "E376", {"start": v(-6.89, -2.43) * mm, "end": v(-7.03, -2.53) * mm});
            skLineSegment(sketch, "E377", {"start": v(-7.03, -2.53) * mm, "end": v(-7.16, -2.63) * mm});
            skLineSegment(sketch, "E378", {"start": v(-7.16, -2.63) * mm, "end": v(-7.29, -2.74) * mm});
            skLineSegment(sketch, "E379", {"start": v(-7.29, -2.74) * mm, "end": v(-7.4, -2.86) * mm});
            skLineSegment(sketch, "E380", {"start": v(-7.4, -2.86) * mm, "end": v(-7.52, -3) * mm});
            skLineSegment(sketch, "E381", {"start": v(-7.52, -3) * mm, "end": v(-7.62, -3.12) * mm});
            skLineSegment(sketch, "E382", {"start": v(-7.62, -3.12) * mm, "end": v(-7.7, -3.27) * mm});
            skLineSegment(sketch, "E383", {"start": v(-7.7, -3.27) * mm, "end": v(-7.8, -3.41) * mm});
            skLineSegment(sketch, "E384", {"start": v(-7.8, -3.41) * mm, "end": v(-7.87, -3.57) * mm});
            skLineSegment(sketch, "E385", {"start": v(-7.87, -3.57) * mm, "end": v(-7.93, -3.72) * mm});
            skLineSegment(sketch, "E386", {"start": v(-7.93, -3.72) * mm, "end": v(-7.98, -3.88) * mm});
            skLineSegment(sketch, "E387", {"start": v(-7.98, -3.88) * mm, "end": v(-8.02, -4.04) * mm});
            skLineSegment(sketch, "E388", {"start": v(-8.02, -4.04) * mm, "end": v(-7.86, -4.09) * mm});
            skLineSegment(sketch, "E389", {"start": v(-7.86, -4.09) * mm, "end": v(-7.7, -4.12) * mm});
            skLineSegment(sketch, "E390", {"start": v(-7.7, -4.12) * mm, "end": v(-7.52, -4.15) * mm});
            skLineSegment(sketch, "E391", {"start": v(-7.52, -4.15) * mm, "end": v(-7.36, -4.16) * mm});
            skLineSegment(sketch, "E392", {"start": v(-7.36, -4.16) * mm, "end": v(-7.19, -4.16) * mm});
            skLineSegment(sketch, "E393", {"start": v(-7.19, -4.16) * mm, "end": v(-7.02, -4.15) * mm});
            skLineSegment(sketch, "E394", {"start": v(-7.02, -4.15) * mm, "end": v(-6.85, -4.13) * mm});
            skLineSegment(sketch, "E395", {"start": v(-6.85, -4.13) * mm, "end": v(-6.69, -4.1) * mm});
            skLineSegment(sketch, "E396", {"start": v(-6.69, -4.1) * mm, "end": v(-6.52, -4.06) * mm});
            skLineSegment(sketch, "E397", {"start": v(-6.52, -4.06) * mm, "end": v(-6.37, -4) * mm});
            skLineSegment(sketch, "E398", {"start": v(-6.37, -4) * mm, "end": v(-6.2, -3.94) * mm});
            skLineSegment(sketch, "E399", {"start": v(-6.2, -3.94) * mm, "end": v(-6.06, -3.87) * mm});
            skLineSegment(sketch, "E400", {"start": v(-6.06, -3.87) * mm, "end": v(-5.93, -3.77) * mm});
            skLineSegment(sketch, "E401", {"start": v(-5.93, -3.77) * mm, "end": v(-5.8, -3.66) * mm});
            skLineSegment(sketch, "E402", {"start": v(-5.8, -3.66) * mm, "end": v(-5.66, -3.56) * mm});
            skLineSegment(sketch, "E403", {"start": v(-5.66, -3.56) * mm, "end": v(-5.53, -3.46) * mm});
            skLineSegment(sketch, "E404", {"start": v(-5.53, -3.46) * mm, "end": v(-5.4, -3.36) * mm});
            skLineSegment(sketch, "E405", {"start": v(-5.4, -3.36) * mm, "end": v(-5.27, -3.26) * mm});
            skLineSegment(sketch, "E406", {"start": v(-5.27, -3.26) * mm, "end": v(-5.13, -3.16) * mm});
            skLineSegment(sketch, "E407", {"start": v(-5.13, -3.16) * mm, "end": v(-5, -3.06) * mm});
            skLineSegment(sketch, "E408", {"start": v(-5, -3.06) * mm, "end": v(-4.87, -2.96) * mm});
            skLineSegment(sketch, "E409", {"start": v(-4.87, -2.96) * mm, "end": v(-4.74, -2.85) * mm});
            skLineSegment(sketch, "E410", {"start": v(-4.74, -2.85) * mm, "end": v(-4.62, -2.98) * mm});
            skLineSegment(sketch, "E411", {"start": v(-4.62, -2.98) * mm, "end": v(-4.5, -3.1) * mm});
            skLineSegment(sketch, "E412", {"start": v(-4.5, -3.1) * mm, "end": v(-4.37, -3.22) * mm});
            skLineSegment(sketch, "E413", {"start": v(-4.37, -3.22) * mm, "end": v(-4.25, -3.34) * mm});
            skLineSegment(sketch, "E414", {"start": v(-4.25, -3.34) * mm, "end": v(-4.13, -3.46) * mm});
            skLineSegment(sketch, "E415", {"start": v(-4.13, -3.46) * mm, "end": v(-4, -3.58) * mm});
            skLineSegment(sketch, "E416", {"start": v(-4, -3.58) * mm, "end": v(-3.89, -3.7) * mm});
            skLineSegment(sketch, "E417", {"start": v(-3.89, -3.7) * mm, "end": v(-3.87, -3.72) * mm});
            skLineSegment(sketch, "E418", {"start": v(-3.87, -3.72) * mm, "end": v(-3.97, -3.85) * mm});
            skLineSegment(sketch, "E419", {"start": v(-3.97, -3.85) * mm, "end": v(-4.07, -3.98) * mm});
            skLineSegment(sketch, "E420", {"start": v(-4.07, -3.98) * mm, "end": v(-4.18, -4.12) * mm});
            skLineSegment(sketch, "E421", {"start": v(-4.18, -4.12) * mm, "end": v(-4.28, -4.25) * mm});
            skLineSegment(sketch, "E422", {"start": v(-4.28, -4.25) * mm, "end": v(-4.38, -4.38) * mm});
            skLineSegment(sketch, "E423", {"start": v(-4.38, -4.38) * mm, "end": v(-4.48, -4.51) * mm});
            skLineSegment(sketch, "E424", {"start": v(-4.48, -4.51) * mm, "end": v(-4.58, -4.64) * mm});
            skLineSegment(sketch, "E425", {"start": v(-4.58, -4.64) * mm, "end": v(-4.68, -4.78) * mm});
            skLineSegment(sketch, "E426", {"start": v(-4.68, -4.78) * mm, "end": v(-4.78, -4.9) * mm});
            skLineSegment(sketch, "E427", {"start": v(-4.78, -4.9) * mm, "end": v(-4.88, -5.04) * mm});
            skLineSegment(sketch, "E428", {"start": v(-4.88, -5.04) * mm, "end": v(-4.96, -5.2) * mm});
            skLineSegment(sketch, "E429", {"start": v(-4.96, -5.2) * mm, "end": v(-5.02, -5.35) * mm});
            skLineSegment(sketch, "E430", {"start": v(-5.02, -5.35) * mm, "end": v(-5.08, -5.51) * mm});
            skLineSegment(sketch, "E431", {"start": v(-5.08, -5.51) * mm, "end": v(-5.12, -5.67) * mm});
            skLineSegment(sketch, "E432", {"start": v(-5.12, -5.67) * mm, "end": v(-5.15, -5.84) * mm});
            skLineSegment(sketch, "E433", {"start": v(-5.15, -5.84) * mm, "end": v(-5.17, -6) * mm});
            skLineSegment(sketch, "E434", {"start": v(-5.17, -6) * mm, "end": v(-5.18, -6.18) * mm});
            skLineSegment(sketch, "E435", {"start": v(-5.18, -6.18) * mm, "end": v(-5.18, -6.34) * mm});
            skLineSegment(sketch, "E436", {"start": v(-5.18, -6.34) * mm, "end": v(-5.16, -6.51) * mm});
            skLineSegment(sketch, "E437", {"start": v(-5.16, -6.51) * mm, "end": v(-5.14, -6.68) * mm});
            skLineSegment(sketch, "E438", {"start": v(-5.14, -6.68) * mm, "end": v(-5.1, -6.85) * mm});
            skLineSegment(sketch, "E439", {"start": v(-5.1, -6.85) * mm, "end": v(-5.06, -7) * mm});
            skLineSegment(sketch, "E440", {"start": v(-5.06, -7) * mm, "end": v(-4.9, -6.96) * mm});
            skLineSegment(sketch, "E441", {"start": v(-4.9, -6.96) * mm, "end": v(-4.74, -6.91) * mm});
            skLineSegment(sketch, "E442", {"start": v(-4.74, -6.91) * mm, "end": v(-4.58, -6.85) * mm});
            skLineSegment(sketch, "E443", {"start": v(-4.58, -6.85) * mm, "end": v(-4.43, -6.77) * mm});
            skLineSegment(sketch, "E444", {"start": v(-4.43, -6.77) * mm, "end": v(-4.28, -6.69) * mm});
            skLineSegment(sketch, "E445", {"start": v(-4.28, -6.69) * mm, "end": v(-4.14, -6.6) * mm});
            skLineSegment(sketch, "E446", {"start": v(-4.14, -6.6) * mm, "end": v(-4, -6.5) * mm});
            skLineSegment(sketch, "E447", {"start": v(-4, -6.5) * mm, "end": v(-3.88, -6.39) * mm});
            skLineSegment(sketch, "E448", {"start": v(-3.88, -6.39) * mm, "end": v(-3.76, -6.27) * mm});
            skLineSegment(sketch, "E449", {"start": v(-3.76, -6.27) * mm, "end": v(-3.65, -6.14) * mm});
            skLineSegment(sketch, "E450", {"start": v(-3.65, -6.14) * mm, "end": v(-3.54, -6) * mm});
            skLineSegment(sketch, "E451", {"start": v(-3.54, -6) * mm, "end": v(-3.45, -5.87) * mm});
            skLineSegment(sketch, "E452", {"start": v(-3.45, -5.87) * mm, "end": v(-3.38, -5.72) * mm});
            skLineSegment(sketch, "E453", {"start": v(-3.38, -5.72) * mm, "end": v(-3.32, -5.56) * mm});
            skLineSegment(sketch, "E454", {"start": v(-3.32, -5.56) * mm, "end": v(-3.26, -5.4) * mm});
            skLineSegment(sketch, "E455", {"start": v(-3.26, -5.4) * mm, "end": v(-3.2, -5.25) * mm});
            skLineSegment(sketch, "E456", {"start": v(-3.2, -5.25) * mm, "end": v(-3.13, -5.1) * mm});
            skLineSegment(sketch, "E457", {"start": v(-3.13, -5.1) * mm, "end": v(-3.07, -4.95) * mm});
            skLineSegment(sketch, "E458", {"start": v(-3.07, -4.95) * mm, "end": v(-3, -4.8) * mm});
            skLineSegment(sketch, "E459", {"start": v(-3, -4.8) * mm, "end": v(-2.94, -4.64) * mm});
            skLineSegment(sketch, "E460", {"start": v(-2.94, -4.64) * mm, "end": v(-2.88, -4.49) * mm});
            skLineSegment(sketch, "E461", {"start": v(-2.88, -4.49) * mm, "end": v(-2.81, -4.33) * mm});
            skLineSegment(sketch, "E462", {"start": v(-2.81, -4.33) * mm, "end": v(-2.65, -4.38) * mm});
            skLineSegment(sketch, "E463", {"start": v(-2.65, -4.38) * mm, "end": v(-2.48, -4.42) * mm});
            skLineSegment(sketch, "E464", {"start": v(-2.48, -4.42) * mm, "end": v(-2.31, -4.47) * mm});
            skLineSegment(sketch, "E465", {"start": v(-2.31, -4.47) * mm, "end": v(-2.15, -4.51) * mm});
            skLineSegment(sketch, "E466", {"start": v(-2.15, -4.51) * mm, "end": v(-1.98, -4.56) * mm});
            skLineSegment(sketch, "E467", {"start": v(-1.98, -4.56) * mm, "end": v(-1.81, -4.6) * mm});
            skLineSegment(sketch, "E468", {"start": v(-1.81, -4.6) * mm, "end": v(-1.65, -4.64) * mm});
            skLineSegment(sketch, "E469", {"start": v(-1.65, -4.64) * mm, "end": v(-1.63, -4.65) * mm});
            skLineSegment(sketch, "E470", {"start": v(-1.63, -4.65) * mm, "end": v(-1.65, -4.81) * mm});
            skLineSegment(sketch, "E471", {"start": v(-1.65, -4.81) * mm, "end": v(-1.67, -4.98) * mm});
            skLineSegment(sketch, "E472", {"start": v(-1.67, -4.98) * mm, "end": v(-1.7, -5.14) * mm});
            skLineSegment(sketch, "E473", {"start": v(-1.7, -5.14) * mm, "end": v(-1.72, -5.3) * mm});
            skLineSegment(sketch, "E474", {"start": v(-1.72, -5.3) * mm, "end": v(-1.74, -5.47) * mm});
            skLineSegment(sketch, "E475", {"start": v(-1.74, -5.47) * mm, "end": v(-1.76, -5.64) * mm});
            skLineSegment(sketch, "E476", {"start": v(-1.76, -5.64) * mm, "end": v(-1.78, -5.8) * mm});
            skLineSegment(sketch, "E477", {"start": v(-1.78, -5.8) * mm, "end": v(-1.8, -5.97) * mm});
            skLineSegment(sketch, "E478", {"start": v(-1.8, -5.97) * mm, "end": v(-1.82, -6.13) * mm});
            skLineSegment(sketch, "E479", {"start": v(-1.82, -6.13) * mm, "end": v(-1.85, -6.3) * mm});
            skLineSegment(sketch, "E480", {"start": v(-1.85, -6.3) * mm, "end": v(-1.83, -6.47) * mm});
            skLineSegment(sketch, "E481", {"start": v(-1.83, -6.47) * mm, "end": v(-1.81, -6.63) * mm});
            skLineSegment(sketch, "E482", {"start": v(-1.81, -6.63) * mm, "end": v(-1.78, -6.8) * mm});
            skLineSegment(sketch, "E483", {"start": v(-1.78, -6.8) * mm, "end": v(-1.73, -6.96) * mm});
            skLineSegment(sketch, "E484", {"start": v(-1.73, -6.96) * mm, "end": v(-1.67, -7.12) * mm});
            skLineSegment(sketch, "E485", {"start": v(-1.67, -7.12) * mm, "end": v(-1.61, -7.28) * mm});
            skLineSegment(sketch, "E486", {"start": v(-1.61, -7.28) * mm, "end": v(-1.53, -7.43) * mm});
            skLineSegment(sketch, "E487", {"start": v(-1.53, -7.43) * mm, "end": v(-1.45, -7.57) * mm});
            skLineSegment(sketch, "E488", {"start": v(-1.45, -7.57) * mm, "end": v(-1.35, -7.71) * mm});
            skLineSegment(sketch, "E489", {"start": v(-1.35, -7.71) * mm, "end": v(-1.25, -7.85) * mm});
            skLineSegment(sketch, "E490", {"start": v(-1.25, -7.85) * mm, "end": v(-1.13, -7.97) * mm});
            skLineSegment(sketch, "E491", {"start": v(-1.13, -7.97) * mm, "end": v(-1.02, -8.09) * mm});
            skLineSegment(sketch, "E492", {"start": v(-1.02, -8.09) * mm, "end": v(-0.9, -7.97) * mm});
            skLineSegment(sketch, "E493", {"start": v(-0.9, -7.97) * mm, "end": v(-0.78, -7.85) * mm});
            skLineSegment(sketch, "E494", {"start": v(-0.78, -7.85) * mm, "end": v(-0.68, -7.7) * mm});
            skLineSegment(sketch, "E495", {"start": v(-0.68, -7.7) * mm, "end": v(-0.58, -7.57) * mm});
            skLineSegment(sketch, "E496", {"start": v(-0.58, -7.57) * mm, "end": v(-0.5, -7.42) * mm});
            skLineSegment(sketch, "E497", {"start": v(-0.5, -7.42) * mm, "end": v(-0.42, -7.28) * mm});
            skLineSegment(sketch, "E498", {"start": v(-0.42, -7.28) * mm, "end": v(-0.36, -7.12) * mm});
            skLineSegment(sketch, "E499", {"start": v(-0.36, -7.12) * mm, "end": v(-0.3, -6.96) * mm});
            skLineSegment(sketch, "E500", {"start": v(-0.3, -6.96) * mm, "end": v(-0.26, -6.8) * mm});
            skLineSegment(sketch, "E501", {"start": v(-0.26, -6.8) * mm, "end": v(-0.22, -6.63) * mm});
            skLineSegment(sketch, "E502", {"start": v(-0.22, -6.63) * mm, "end": v(-0.2, -6.46) * mm});
            skLineSegment(sketch, "E503", {"start": v(-0.2, -6.46) * mm, "end": v(-0.19, -6.3) * mm});
            skLineSegment(sketch, "E504", {"start": v(-0.19, -6.3) * mm, "end": v(-0.2, -6.13) * mm});
            skLineSegment(sketch, "E505", {"start": v(-0.2, -6.13) * mm, "end": v(-0.23, -5.97) * mm});
            skLineSegment(sketch, "E506", {"start": v(-0.23, -5.97) * mm, "end": v(-0.25, -5.8) * mm});
            skLineSegment(sketch, "E507", {"start": v(-0.25, -5.8) * mm, "end": v(-0.27, -5.64) * mm});
            skLineSegment(sketch, "E508", {"start": v(-0.27, -5.64) * mm, "end": v(-0.3, -5.47) * mm});
            skLineSegment(sketch, "E509", {"start": v(-0.3, -5.47) * mm, "end": v(-0.32, -5.3) * mm});
            skLineSegment(sketch, "E510", {"start": v(-0.32, -5.3) * mm, "end": v(-0.34, -5.14) * mm});
            skLineSegment(sketch, "E511", {"start": v(-0.34, -5.14) * mm, "end": v(-0.36, -4.98) * mm});
            skLineSegment(sketch, "E512", {"start": v(-0.36, -4.98) * mm, "end": v(-0.38, -4.81) * mm});
            skLineSegment(sketch, "E513", {"start": v(-0.38, -4.81) * mm, "end": v(-0.4, -4.65) * mm});
            skLineSegment(sketch, "E514", {"start": v(-0.4, -4.65) * mm, "end": v(-0.24, -4.6) * mm});
            skLineSegment(sketch, "E515", {"start": v(-0.24, -4.6) * mm, "end": v(-0.07, -4.56) * mm});
            skLineSegment(sketch, "E516", {"start": v(-0.07, -4.56) * mm, "end": v(0.1, -4.52) * mm});
            skLineSegment(sketch, "E517", {"start": v(0.1, -4.52) * mm, "end": v(0.26, -4.47) * mm});
            skLineSegment(sketch, "E518", {"start": v(0.26, -4.47) * mm, "end": v(0.43, -4.43) * mm});
            skLineSegment(sketch, "E519", {"start": v(0.43, -4.43) * mm, "end": v(0.6, -4.38) * mm});
            skLineSegment(sketch, "E520", {"start": v(0.6, -4.38) * mm, "end": v(0.76, -4.34) * mm});
            skLineSegment(sketch, "E521", {"start": v(0.76, -4.34) * mm, "end": v(0.78, -4.33) * mm});
            skLineSegment(sketch, "E522", {"start": v(0.78, -4.33) * mm, "end": v(0.84, -4.49) * mm});
            skLineSegment(sketch, "E523", {"start": v(0.84, -4.49) * mm, "end": v(0.9, -4.64) * mm});
            skLineSegment(sketch, "E524", {"start": v(0.9, -4.64) * mm, "end": v(0.97, -4.8) * mm});
            skLineSegment(sketch, "E525", {"start": v(0.97, -4.8) * mm, "end": v(1.03, -4.95) * mm});
            skLineSegment(sketch, "E526", {"start": v(1.03, -4.95) * mm, "end": v(1.1, -5.1) * mm});
            skLineSegment(sketch, "E527", {"start": v(1.1, -5.1) * mm, "end": v(1.16, -5.25) * mm});
            skLineSegment(sketch, "E528", {"start": v(1.16, -5.25) * mm, "end": v(1.22, -5.4) * mm});
            skLineSegment(sketch, "E529", {"start": v(1.22, -5.4) * mm, "end": v(1.29, -5.56) * mm});
            skLineSegment(sketch, "E530", {"start": v(1.29, -5.56) * mm, "end": v(1.35, -5.72) * mm});
            skLineSegment(sketch, "E531", {"start": v(1.35, -5.72) * mm, "end": v(1.41, -5.87) * mm});
            skLineSegment(sketch, "E532", {"start": v(1.41, -5.87) * mm, "end": v(1.51, -6.01) * mm});
            skLineSegment(sketch, "E533", {"start": v(1.51, -6.01) * mm, "end": v(1.61, -6.14) * mm});
            skLineSegment(sketch, "E534", {"start": v(1.61, -6.14) * mm, "end": v(1.73, -6.27) * mm});
            skLineSegment(sketch, "E535", {"start": v(1.73, -6.27) * mm, "end": v(1.84, -6.39) * mm});
            skLineSegment(sketch, "E536", {"start": v(1.84, -6.39) * mm, "end": v(1.98, -6.5) * mm});
            skLineSegment(sketch, "E537", {"start": v(1.98, -6.5) * mm, "end": v(2.1, -6.6) * mm});
            skLineSegment(sketch, "E538", {"start": v(2.1, -6.6) * mm, "end": v(2.25, -6.7) * mm});
            skLineSegment(sketch, "E539", {"start": v(2.25, -6.7) * mm, "end": v(2.4, -6.77) * mm});
            skLineSegment(sketch, "E540", {"start": v(2.4, -6.77) * mm, "end": v(2.55, -6.85) * mm});
            skLineSegment(sketch, "E541", {"start": v(2.55, -6.85) * mm, "end": v(2.7, -6.91) * mm});
            skLineSegment(sketch, "E542", {"start": v(2.7, -6.91) * mm, "end": v(2.87, -6.96) * mm});
            skLineSegment(sketch, "E543", {"start": v(2.87, -6.96) * mm, "end": v(3.03, -7) * mm});
            skLineSegment(sketch, "E544", {"start": v(3.03, -7) * mm, "end": v(3.07, -6.84) * mm});
            skLineSegment(sketch, "E545", {"start": v(3.07, -6.84) * mm, "end": v(3.1, -6.68) * mm});
            skLineSegment(sketch, "E546", {"start": v(3.1, -6.68) * mm, "end": v(3.13, -6.5) * mm});
            skLineSegment(sketch, "E547", {"start": v(3.13, -6.5) * mm, "end": v(3.14, -6.34) * mm});
            skLineSegment(sketch, "E548", {"start": v(3.14, -6.34) * mm, "end": v(3.14, -6.17) * mm});
            skLineSegment(sketch, "E549", {"start": v(3.14, -6.17) * mm, "end": v(3.14, -6) * mm});
            skLineSegment(sketch, "E550", {"start": v(3.14, -6) * mm, "end": v(3.11, -5.83) * mm});
            skLineSegment(sketch, "E551", {"start": v(3.11, -5.83) * mm, "end": v(3.08, -5.67) * mm});
            skLineSegment(sketch, "E552", {"start": v(3.08, -5.67) * mm, "end": v(3.04, -5.5) * mm});
            skLineSegment(sketch, "E553", {"start": v(3.04, -5.5) * mm, "end": v(2.99, -5.35) * mm});
            skLineSegment(sketch, "E554", {"start": v(2.99, -5.35) * mm, "end": v(2.92, -5.19) * mm});
            skLineSegment(sketch, "E555", {"start": v(2.92, -5.19) * mm, "end": v(2.85, -5.04) * mm});
            skLineSegment(sketch, "E556", {"start": v(2.85, -5.04) * mm, "end": v(2.75, -4.9) * mm});
            skLineSegment(sketch, "E557", {"start": v(2.75, -4.9) * mm, "end": v(2.65, -4.78) * mm});
            skLineSegment(sketch, "E558", {"start": v(2.65, -4.78) * mm, "end": v(2.55, -4.64) * mm});
            skLineSegment(sketch, "E559", {"start": v(2.55, -4.64) * mm, "end": v(2.45, -4.51) * mm});
            skLineSegment(sketch, "E560", {"start": v(2.45, -4.51) * mm, "end": v(2.34, -4.38) * mm});
            skLineSegment(sketch, "E561", {"start": v(2.34, -4.38) * mm, "end": v(2.24, -4.25) * mm});
            skLineSegment(sketch, "E562", {"start": v(2.24, -4.25) * mm, "end": v(2.14, -4.12) * mm});
            skLineSegment(sketch, "E563", {"start": v(2.14, -4.12) * mm, "end": v(2.04, -3.98) * mm});
            skLineSegment(sketch, "E564", {"start": v(2.04, -3.98) * mm, "end": v(1.94, -3.85) * mm});
            skLineSegment(sketch, "E565", {"start": v(1.94, -3.85) * mm, "end": v(1.84, -3.72) * mm});
            skLineSegment(sketch, "E566", {"start": v(1.84, -3.72) * mm, "end": v(1.96, -3.6) * mm});
            skLineSegment(sketch, "E567", {"start": v(1.96, -3.6) * mm, "end": v(2.08, -3.48) * mm});
            skLineSegment(sketch, "E568", {"start": v(2.08, -3.48) * mm, "end": v(2.2, -3.36) * mm});
            skLineSegment(sketch, "E569", {"start": v(2.2, -3.36) * mm, "end": v(2.32, -3.23) * mm});
            skLineSegment(sketch, "E570", {"start": v(2.32, -3.23) * mm, "end": v(2.45, -3.11) * mm});
            skLineSegment(sketch, "E571", {"start": v(2.45, -3.11) * mm, "end": v(2.57, -3) * mm});
            skLineSegment(sketch, "E572", {"start": v(2.57, -3) * mm, "end": v(2.69, -2.87) * mm});
            skLineSegment(sketch, "E573", {"start": v(2.69, -2.87) * mm, "end": v(2.7, -2.85) * mm});
            skLineSegment(sketch, "E574", {"start": v(2.7, -2.85) * mm, "end": v(2.84, -2.96) * mm});
            skLineSegment(sketch, "E575", {"start": v(2.84, -2.96) * mm, "end": v(2.97, -3.06) * mm});
            skLineSegment(sketch, "E576", {"start": v(2.97, -3.06) * mm, "end": v(3.1, -3.16) * mm});
            skLineSegment(sketch, "E577", {"start": v(3.1, -3.16) * mm, "end": v(3.23, -3.26) * mm});
            skLineSegment(sketch, "E578", {"start": v(3.23, -3.26) * mm, "end": v(3.36, -3.36) * mm});
            skLineSegment(sketch, "E579", {"start": v(3.36, -3.36) * mm, "end": v(3.5, -3.46) * mm});
            skLineSegment(sketch, "E580", {"start": v(3.5, -3.46) * mm, "end": v(3.63, -3.56) * mm});
            skLineSegment(sketch, "E581", {"start": v(3.63, -3.56) * mm, "end": v(3.76, -3.66) * mm});
            skLineSegment(sketch, "E582", {"start": v(3.76, -3.66) * mm, "end": v(3.9, -3.77) * mm});
            skLineSegment(sketch, "E583", {"start": v(3.9, -3.77) * mm, "end": v(4.02, -3.87) * mm});
            skLineSegment(sketch, "E584", {"start": v(4.02, -3.87) * mm, "end": v(4.18, -3.94) * mm});
            skLineSegment(sketch, "E585", {"start": v(4.18, -3.94) * mm, "end": v(4.33, -4) * mm});
            skLineSegment(sketch, "E586", {"start": v(4.33, -4) * mm, "end": v(4.5, -4.06) * mm});
            skLineSegment(sketch, "E587", {"start": v(4.5, -4.06) * mm, "end": v(4.65, -4.1) * mm});
            skLineSegment(sketch, "E588", {"start": v(4.65, -4.1) * mm, "end": v(4.82, -4.13) * mm});
            skLineSegment(sketch, "E589", {"start": v(4.82, -4.13) * mm, "end": v(4.99, -4.15) * mm});
            skLineSegment(sketch, "E590", {"start": v(4.99, -4.15) * mm, "end": v(5.16, -4.16) * mm});
            skLineSegment(sketch, "E591", {"start": v(5.16, -4.16) * mm, "end": v(5.33, -4.16) * mm});
            skLineSegment(sketch, "E592", {"start": v(5.33, -4.16) * mm, "end": v(5.5, -4.15) * mm});
            skLineSegment(sketch, "E593", {"start": v(5.5, -4.15) * mm, "end": v(5.66, -4.12) * mm});
            skLineSegment(sketch, "E594", {"start": v(5.66, -4.12) * mm, "end": v(5.83, -4.09) * mm});
            skLineSegment(sketch, "E595", {"start": v(5.83, -4.09) * mm, "end": v(5.99, -4.04) * mm});
            skLineSegment(sketch, "E596", {"start": v(5.99, -4.04) * mm, "end": v(5.94, -3.88) * mm});
            skLineSegment(sketch, "E597", {"start": v(5.94, -3.88) * mm, "end": v(5.9, -3.72) * mm});
            skLineSegment(sketch, "E598", {"start": v(5.9, -3.72) * mm, "end": v(5.83, -3.56) * mm});
            skLineSegment(sketch, "E599", {"start": v(5.83, -3.56) * mm, "end": v(5.76, -3.41) * mm});
            skLineSegment(sketch, "E600", {"start": v(5.76, -3.41) * mm, "end": v(5.67, -3.26) * mm});
            skLineSegment(sketch, "E601", {"start": v(5.67, -3.26) * mm, "end": v(5.58, -3.12) * mm});
            skLineSegment(sketch, "E602", {"start": v(5.58, -3.12) * mm, "end": v(5.48, -2.99) * mm});
            skLineSegment(sketch, "E603", {"start": v(5.48, -2.99) * mm, "end": v(5.37, -2.86) * mm});
            skLineSegment(sketch, "E604", {"start": v(5.37, -2.86) * mm, "end": v(5.25, -2.74) * mm});
            skLineSegment(sketch, "E605", {"start": v(5.25, -2.74) * mm, "end": v(5.13, -2.63) * mm});
            skLineSegment(sketch, "E606", {"start": v(5.13, -2.63) * mm, "end": v(4.99, -2.52) * mm});
            skLineSegment(sketch, "E607", {"start": v(4.99, -2.52) * mm, "end": v(4.85, -2.43) * mm});
            skLineSegment(sketch, "E608", {"start": v(4.85, -2.43) * mm, "end": v(4.7, -2.37) * mm});
            skLineSegment(sketch, "E609", {"start": v(4.7, -2.37) * mm, "end": v(4.55, -2.3) * mm});
            skLineSegment(sketch, "E610", {"start": v(4.55, -2.3) * mm, "end": v(4.4, -2.24) * mm});
            skLineSegment(sketch, "E611", {"start": v(4.4, -2.24) * mm, "end": v(4.24, -2.18) * mm});
            skLineSegment(sketch, "E612", {"start": v(4.24, -2.18) * mm, "end": v(4.08, -2.11) * mm});
            skLineSegment(sketch, "E613", {"start": v(4.08, -2.11) * mm, "end": v(3.93, -2.05) * mm});
            skLineSegment(sketch, "E614", {"start": v(3.93, -2.05) * mm, "end": v(3.78, -1.99) * mm});
            skLineSegment(sketch, "E615", {"start": v(3.78, -1.99) * mm, "end": v(3.62, -1.92) * mm});
            skLineSegment(sketch, "E616", {"start": v(3.62, -1.92) * mm, "end": v(3.47, -1.86) * mm});
            skLineSegment(sketch, "E617", {"start": v(3.47, -1.86) * mm, "end": v(3.32, -1.8) * mm});
            skLineSegment(sketch, "E618", {"start": v(3.32, -1.8) * mm, "end": v(3.36, -1.63) * mm});
            skLineSegment(sketch, "E619", {"start": v(3.36, -1.63) * mm, "end": v(3.4, -1.46) * mm});
            skLineSegment(sketch, "E620", {"start": v(3.4, -1.46) * mm, "end": v(3.45, -1.3) * mm});
            skLineSegment(sketch, "E621", {"start": v(3.45, -1.3) * mm, "end": v(3.5, -1.13) * mm});
            skLineSegment(sketch, "E622", {"start": v(3.5, -1.13) * mm, "end": v(3.54, -0.96) * mm});
            skLineSegment(sketch, "E623", {"start": v(3.54, -0.96) * mm, "end": v(3.58, -0.8) * mm});
            skLineSegment(sketch, "E624", {"start": v(3.58, -0.8) * mm, "end": v(3.63, -0.63) * mm});
            skLineSegment(sketch, "E625", {"start": v(3.63, -0.63) * mm, "end": v(3.63, -0.61) * mm});
            skPoint(sketch, "E626", {"position": v(-1.02, 0) * mm});
            skPoint(sketch, "E627", {"position": v(-1.02, -1) * mm});
            skLineSegment(sketch, "E628", {"start": v(-2.14, -1) * mm, "end": v(0.1, -1) * mm});
            skCircle(sketch, "E629", {"center": v(-1.02, 0) * mm, "radius": 1.5 * mm});
            skSolve(sketch);
        }
        {
            var Q0;
            Q0=makeQuery(id+"F0.imprint","IMPRINT",FACE,{"disambiguationData":[TD([[makeQuery(id+"F0.imprint","IMPRINT",EDGE,{"derivedFrom":sQuery(id+"F0.wireOp",EDGE,"E0")}),1.0]])]});
            var Q1;
            {var subQ0=sQuery(id+"F0.wireOp",EDGE,"E628");Q1=makeQuery(id+"F0.imprint","IMPRINT",FACE,{"disambiguationData":[TD([[makeQuery(id+"F0.imprint","IMPRINT",EDGE,{"derivedFrom":subQ0}),-1.0]])]});}
            extrude(context, id + "F1", {"entities" : qUnion([Q0, Q1]), "depth" : 7 * mm});
        }
    });
